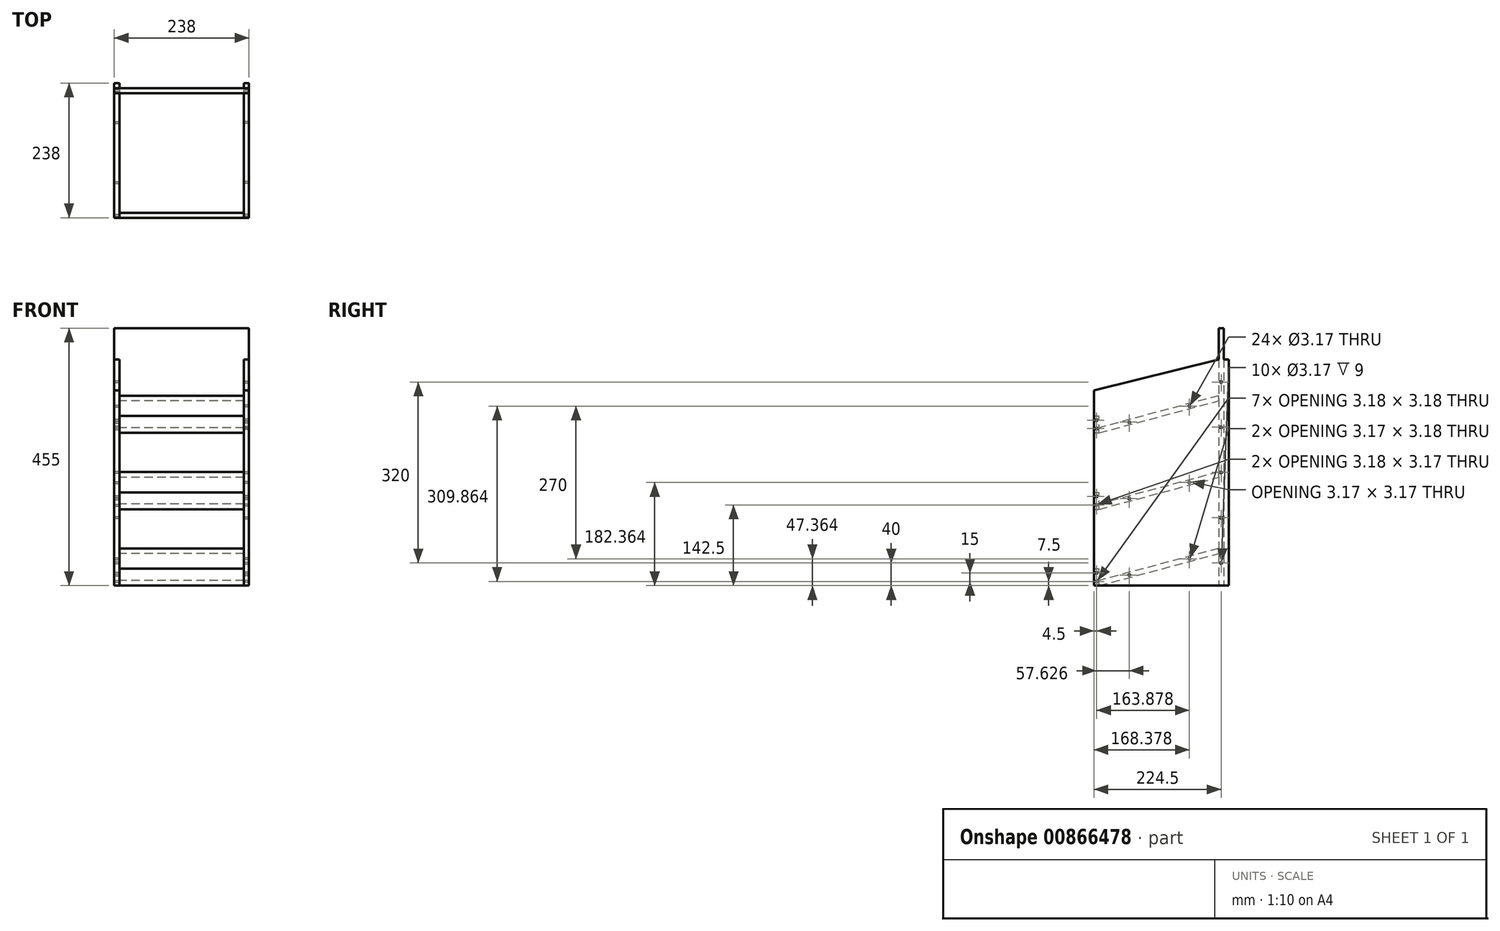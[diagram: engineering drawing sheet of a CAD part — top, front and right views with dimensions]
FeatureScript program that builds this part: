
annotation { "Feature Type Name" : "Feature", "Feature Type Description" : "" }
export const myFeature = defineFeature(function(context is Context, id is Id, definition is map)
    precondition{}
    {
        {
            var Q0;
            Q0=qCreatedBy(makeId("Front.planeOp"),FACE);
            var sketch = newSketch(context, id + "F0", { "sketchPlane" : qUnion([Q0])});
            skLineSegment(sketch, "E0", {"start": v(0, 0) * mm, "end": v(0, -257.67) * mm, "construction": true});
            skLineSegment(sketch, "E1.bottom", {"start": v(110, 165) * mm, "end": v(-110, 165) * mm, "construction": true});
            skLineSegment(sketch, "E1.top", {"start": v(110, -165) * mm, "end": v(-110, -165) * mm, "construction": true});
            skLineSegment(sketch, "E1.left", {"start": v(110, 165) * mm, "end": v(110, -165) * mm, "construction": true});
            skLineSegment(sketch, "E1.right", {"start": v(-110, 165) * mm, "end": v(-110, -165) * mm, "construction": true});
            skPoint(sketch, "E1.middle", {"position": v(0, 0) * mm});
            skLineSegment(sketch, "E2.bottom", {"start": v(-110, -165) * mm, "end": v(-119, -165) * mm});
            skLineSegment(sketch, "E2.top", {"start": v(-110, 235) * mm, "end": v(-119, 235) * mm});
            skLineSegment(sketch, "E2.left", {"start": v(-110, -165) * mm, "end": v(-110, 235) * mm});
            skLineSegment(sketch, "E2.right", {"start": v(-119, -165) * mm, "end": v(-119, 235) * mm});
            skSolve(sketch);
        }
        {
            var Q0;
            Q0=makeQuery(id+"F0.imprint","IMPRINT",FACE,{"disambiguationData":[TD([[makeQuery(id+"F0.imprint","IMPRINT",EDGE,{"derivedFrom":sQuery(id+"F0.wireOp",EDGE,"E2.bottom")}),-1.0]])]});
            var Q1;
            Q1=makeQuery(id+"F0.imprint","IMPRINT",FACE,{"disambiguationData":[TD([[makeQuery(id+"F0.imprint","IMPRINT",EDGE,{"derivedFrom":sQuery(id+"F0.wireOp",EDGE,"DBtvyfOU-g9G0-gBuZ-INMD-cw8ts6dnQgd4.bottom")}),1.0]])]});
            extrude(context, id + "F1", {"entities" : qUnion([Q0, Q1]), "depth" : 238 * mm, "offsetDistance" : 25 * mm});
        }
        {
            var Q0;
            Q0=makeQuery(id+"F1.opExtrude","SWEPT_FACE",FACE,{"disambiguationData":[OSD([sQuery(id+"F0.wireOp",EDGE,"E2.right")])]});
            var sketch = newSketch(context, id + "F2", { "sketchPlane" : qUnion([Q0])});
            skLineSegment(sketch, "E3", {"start": v(238, 235) * mm, "end": v(238, 180) * mm});
            skLineSegment(sketch, "E4", {"start": v(238, 180) * mm, "end": v(18, 235) * mm});
            skLineSegment(sketch, "E5", {"start": v(18, 235) * mm, "end": v(238, 235) * mm});
            skSolve(sketch);
        }
        {
            var Q0;
            Q0=makeQuery(id+"F2.imprint","IMPRINT",FACE,{"disambiguationData":[TD([[makeQuery(id+"F2.imprint","IMPRINT",EDGE,{"derivedFrom":sQuery(id+"F2.wireOp",EDGE,"E3")}),1.0]])]});
            extrude(context, id + "F3", {"entities" : qUnion([Q0]), "operationType" : NewBodyOperationType.REMOVE, "oppositeDirection" : true, "depth" : 10 * mm, "offsetDistance" : 25 * mm});
        }
        {
            var Q0;
            Q0=makeQuery(id+"F1.opExtrude","SWEPT_FACE",FACE,{"disambiguationData":[OSD([sQuery(id+"F0.wireOp",EDGE,"E2.right")])]});
            var sketch = newSketch(context, id + "F4", { "sketchPlane" : qUnion([Q0])});
            skLineSegment(sketch, "E6.bottom", {"start": v(18, 235) * mm, "end": v(9, 235) * mm, "construction": true});
            skLineSegment(sketch, "E6.top", {"start": v(18, -165) * mm, "end": v(9, -165) * mm, "construction": true});
            skLineSegment(sketch, "E6.left", {"start": v(18, 235) * mm, "end": v(18, -165) * mm, "construction": true});
            skLineSegment(sketch, "E6.right", {"start": v(9, 235) * mm, "end": v(9, -165) * mm, "construction": true});
            skCircle(sketch, "E7", {"center": v(13.5, 195) * mm, "radius": 1.59 * mm});
            skCircle(sketch, "E8.0.1.0", {"center": v(13.5, 115) * mm, "radius": 1.59 * mm});
            skCircle(sketch, "E8.0.2.0", {"center": v(13.5, 35) * mm, "radius": 1.59 * mm});
            skLineSegment(sketch, "E8.direction1", {"start": v(13.5, 195) * mm, "end": v(40.5, 195) * mm, "construction": true});
            skLineSegment(sketch, "E8.direction2", {"start": v(13.5, 195) * mm, "end": v(13.5, 115) * mm, "construction": true});
            skCircle(sketch, "E9.0.0.3", {"center": v(13.5, -45) * mm, "radius": 1.59 * mm});
            skCircle(sketch, "E9.0.0.4", {"center": v(13.5, -125) * mm, "radius": 1.59 * mm});
            skSolve(sketch);
        }
        {
            var Q0;
            Q0 = qSketchRegion(id + "F4", true);
            extrude(context, id + "F5", {"entities" : qUnion([Q0]), "operationType" : NewBodyOperationType.REMOVE, "oppositeDirection" : true, "depth" : 9 * mm, "offsetDistance" : 25 * mm});
        }
        {
            var Q0;
            Q0=makeQuery(id+"F1.opExtrude","SWEPT_FACE",FACE,{"disambiguationData":[OSD([sQuery(id+"F0.wireOp",EDGE,"E2.left")])]});
            var sketch = newSketch(context, id + "F6", { "sketchPlane" : qUnion([Q0])});
            skLineSegment(sketch, "E10.bottom", {"start": v(-238, -165) * mm, "end": v(-229, -165) * mm, "construction": true});
            skLineSegment(sketch, "E10.top", {"start": v(-238, 180) * mm, "end": v(-229, 180) * mm, "construction": true});
            skLineSegment(sketch, "E10.left", {"start": v(-238, -165) * mm, "end": v(-238, 180) * mm, "construction": true});
            skLineSegment(sketch, "E10.right", {"start": v(-229, -165) * mm, "end": v(-229, 180) * mm, "construction": true});
            skPoint(sketch, "E11.oppositeSnap0", {"position": v(-9, 235) * mm});
            skLineSegment(sketch, "E11.bottom", {"start": v(-18, 235) * mm, "end": v(-9, 235) * mm, "construction": true});
            skLineSegment(sketch, "E11.top", {"start": v(-18, -165) * mm, "end": v(-9, -165) * mm, "construction": true});
            skLineSegment(sketch, "E11.left", {"start": v(-18, 235) * mm, "end": v(-18, -165) * mm, "construction": true});
            skLineSegment(sketch, "E11.right", {"start": v(-9, 235) * mm, "end": v(-9, -165) * mm, "construction": true});
            skLineSegment(sketch, "E12", {"start": v(-229, -165) * mm, "end": v(-18, -108.46) * mm, "construction": true});
            skLineSegment(sketch, "E13", {"start": v(-229, -155.68) * mm, "end": v(-18, -99.15) * mm, "construction": true});
            skLineSegment(sketch, "E14", {"start": v(-229, -155.68) * mm, "end": v(-229, -165) * mm, "construction": true});
            skLineSegment(sketch, "E15", {"start": v(-18, -99.15) * mm, "end": v(-18, -108.46) * mm, "construction": true});
            skLineSegment(sketch, "E16", {"start": v(-229, -160.34) * mm, "end": v(-18, -103.8) * mm, "construction": true});
            skCircle(sketch, "E17", {"center": v(-175.87, -146.1) * mm, "radius": 1.59 * mm});
            skLineSegment(sketch, "E18", {"start": v(-229, -30) * mm, "end": v(-18, 26.54) * mm, "construction": true});
            skLineSegment(sketch, "E19", {"start": v(-229, -30) * mm, "end": v(-229, -20.68) * mm, "construction": true});
            skLineSegment(sketch, "E20", {"start": v(-229, -20.68) * mm, "end": v(-18, 35.85) * mm, "construction": true});
            skLineSegment(sketch, "E21", {"start": v(-18, 35.85) * mm, "end": v(-18, 26.54) * mm, "construction": true});
            skLineSegment(sketch, "E22", {"start": v(-229, -25.34) * mm, "end": v(-18, 31.2) * mm, "construction": true});
            skCircle(sketch, "E23", {"center": v(-175.87, -11.1) * mm, "radius": 1.59 * mm});
            skLineSegment(sketch, "E24", {"start": v(-229, 105) * mm, "end": v(-18, 161.54) * mm, "construction": true});
            skLineSegment(sketch, "E25", {"start": v(-229, 105) * mm, "end": v(-229, 114.32) * mm, "construction": true});
            skLineSegment(sketch, "E26", {"start": v(-229, 114.32) * mm, "end": v(-18, 170.85) * mm, "construction": true});
            skLineSegment(sketch, "E27", {"start": v(-18, 170.85) * mm, "end": v(-18, 161.54) * mm, "construction": true});
            skLineSegment(sketch, "E28", {"start": v(-229, 109.66) * mm, "end": v(-18, 166.2) * mm, "construction": true});
            skCircle(sketch, "E29", {"center": v(-175.87, 123.9) * mm, "radius": 1.59 * mm});
            skCircle(sketch, "E30", {"center": v(-69.62, 152.36) * mm, "radius": 1.59 * mm});
            skCircle(sketch, "E31", {"center": v(-69.62, 17.36) * mm, "radius": 1.59 * mm});
            skCircle(sketch, "E32", {"center": v(-69.62, -117.64) * mm, "radius": 1.59 * mm});
            skLineSegment(sketch, "E33.bottom", {"start": v(-229, 105) * mm, "end": v(-238, 105) * mm, "construction": true});
            skLineSegment(sketch, "E33.top", {"start": v(-229, 135) * mm, "end": v(-238, 135) * mm, "construction": true});
            skLineSegment(sketch, "E33.left", {"start": v(-229, 105) * mm, "end": v(-229, 135) * mm, "construction": true});
            skLineSegment(sketch, "E33.right", {"start": v(-238, 105) * mm, "end": v(-238, 135) * mm, "construction": true});
            skLineSegment(sketch, "E34.bottom", {"start": v(-229, -30) * mm, "end": v(-238, -30) * mm, "construction": true});
            skLineSegment(sketch, "E34.top", {"start": v(-229, 0) * mm, "end": v(-238, 0) * mm, "construction": true});
            skLineSegment(sketch, "E34.left", {"start": v(-229, -30) * mm, "end": v(-229, 0) * mm, "construction": true});
            skLineSegment(sketch, "E34.right", {"start": v(-238, -30) * mm, "end": v(-238, 0) * mm, "construction": true});
            skLineSegment(sketch, "E35.bottom", {"start": v(-229, -165) * mm, "end": v(-238, -165) * mm, "construction": true});
            skLineSegment(sketch, "E35.top", {"start": v(-229, -135) * mm, "end": v(-238, -135) * mm, "construction": true});
            skLineSegment(sketch, "E35.left", {"start": v(-229, -165) * mm, "end": v(-229, -135) * mm, "construction": true});
            skLineSegment(sketch, "E35.right", {"start": v(-238, -165) * mm, "end": v(-238, -135) * mm, "construction": true});
            skLineSegment(sketch, "E36", {"start": v(-233.5, 135) * mm, "end": v(-233.5, -165) * mm, "construction": true});
            skCircle(sketch, "E37", {"center": v(-233.5, -142.5) * mm, "radius": 1.59 * mm});
            skCircle(sketch, "E38", {"center": v(-233.5, -157.5) * mm, "radius": 1.59 * mm});
            skCircle(sketch, "E39", {"center": v(-233.5, -7.5) * mm, "radius": 1.59 * mm});
            skCircle(sketch, "E40", {"center": v(-233.5, -22.5) * mm, "radius": 1.59 * mm});
            skCircle(sketch, "E41", {"center": v(-233.5, 127.5) * mm, "radius": 1.59 * mm});
            skCircle(sketch, "E42", {"center": v(-233.5, 112.5) * mm, "radius": 1.59 * mm});
            skSolve(sketch);
        }
        {
            var Q0;
            Q0 = qSketchRegion(id + "F6", true);
            extrude(context, id + "F7", {"entities" : qUnion([Q0]), "operationType" : NewBodyOperationType.REMOVE, "oppositeDirection" : true, "depth" : 25 * mm, "offsetDistance" : 25 * mm});
        }
        {
            var Q0;
            Q0=makeQuery(id+"F1.opExtrude","SWEPT_BODY",BODY,{"disambiguationData":[OSD([sQuery(id+"F0.wireOp",EDGE,"E2.bottom"),sQuery(id+"F0.wireOp",EDGE,"E2.top"),sQuery(id+"F0.wireOp",EDGE,"E2.left"),sQuery(id+"F0.wireOp",EDGE,"E2.right")])]});
            var Q1;
            Q1=qCreatedBy(makeId("Right.planeOp"),FACE);
            mirror(context, id + "F8", {"entities" : qUnion([Q0]), "mirrorPlane" : qUnion([Q1])});
        }
        {
            var Q0;
            Q0=makeQuery(id+"F8.opPattern","COPY",FACE,{"derivedFrom":makeQuery(id+"F1.opExtrude","SWEPT_FACE",FACE,{"disambiguationData":[OSD([sQuery(id+"F0.wireOp",EDGE,"E2.bottom")])]}),"instanceName":"1"});
            var sketch = newSketch(context, id + "F9", { "sketchPlane" : qUnion([Q0])});
            skLineSegment(sketch, "E43.bottom", {"start": v(110, 9) * mm, "end": v(-110, 9) * mm});
            skLineSegment(sketch, "E43.top", {"start": v(110, 18) * mm, "end": v(-110, 18) * mm});
            skLineSegment(sketch, "E43.left", {"start": v(110, 9) * mm, "end": v(110, 18) * mm});
            skLineSegment(sketch, "E43.right", {"start": v(-110, 9) * mm, "end": v(-110, 18) * mm});
            skPoint(sketch, "E43.middle", {"position": v(0, 13.5) * mm});
            skSolve(sketch);
        }
        {
            var Q0;
            Q0=makeQuery(id+"F9.imprint","IMPRINT",FACE,{"disambiguationData":[TD([[makeQuery(id+"F9.imprint","IMPRINT",EDGE,{"derivedFrom":sQuery(id+"F9.wireOp",EDGE,"E43.bottom")}),-1.0]])]});
            extrude(context, id + "F10", {"entities" : qUnion([Q0]), "oppositeDirection" : true, "depth" : 400 * mm, "offsetDistance" : 25 * mm});
        }
        {
            var Q0;
            Q0=makeQuery(id+"F10.opExtrude","CAP_FACE",FACE,{"disambiguationData":[OSD([sQuery(id+"F9.wireOp",EDGE,"E43.bottom"),sQuery(id+"F9.wireOp",EDGE,"E43.top"),sQuery(id+"F9.wireOp",EDGE,"E43.left"),sQuery(id+"F9.wireOp",EDGE,"E43.right")])],"isStart":false});
            var sketch = newSketch(context, id + "F11", { "sketchPlane" : qUnion([Q0])});
            skLineSegment(sketch, "E44.bottom", {"start": v(119, -9) * mm, "end": v(-119, -9) * mm});
            skLineSegment(sketch, "E44.top", {"start": v(119, -18) * mm, "end": v(-119, -18) * mm});
            skLineSegment(sketch, "E44.left", {"start": v(119, -9) * mm, "end": v(119, -18) * mm});
            skLineSegment(sketch, "E44.right", {"start": v(-119, -9) * mm, "end": v(-119, -18) * mm});
            skPoint(sketch, "E44.middle", {"position": v(0, -13.5) * mm});
            skPoint(sketch, "E44.middle.positionSnap0", {"position": v(0, -9) * mm});
            skPoint(sketch, "E44.centerSnap0", {"position": v(0, -9) * mm});
            skSolve(sketch);
        }
        {
            var Q0;
            {var subQ1=makeQuery(id+"F10.opExtrude","CAP_EDGE",EDGE,{"disambiguationData":[OSD([sQuery(id+"F9.wireOp",EDGE,"E43.left")])],"isStart":false});Q0=makeQuery(id+"F11.imprint","IMPRINT",FACE,{"disambiguationData":[TD([[makeQuery(id+"F11.imprint","IMPRINT",EDGE,{"derivedFrom":subQ1}),1.0]])]});}
            var Q1;
            {var subQ2=sQuery(id+"F11.wireOp",EDGE,"E44.right");Q1=makeQuery(id+"F11.imprint","IMPRINT",FACE,{"disambiguationData":[TD([[makeQuery(id+"F11.imprint","IMPRINT",EDGE,{"derivedFrom":subQ2}),1.0]])]});}
            var Q2;
            {var subQ2=sQuery(id+"F11.wireOp",EDGE,"E44.left");Q2=makeQuery(id+"F11.imprint","IMPRINT",FACE,{"disambiguationData":[TD([[makeQuery(id+"F11.imprint","IMPRINT",EDGE,{"derivedFrom":subQ2}),-1.0]])]});}
            extrude(context, id + "F12", {"entities" : qUnion([Q0, Q1, Q2]), "operationType" : NewBodyOperationType.ADD, "depth" : 55 * mm, "offsetDistance" : 25 * mm});
        }
        {
            var Q0;
            Q0=makeQuery(id+"F1.opExtrude","SWEPT_FACE",FACE,{"disambiguationData":[OSD([sQuery(id+"F0.wireOp",EDGE,"E2.left")])]});
            var sketch = newSketch(context, id + "F13", { "sketchPlane" : qUnion([Q0])});
            skLineSegment(sketch, "E45.bottom", {"start": v(-238, -165) * mm, "end": v(-229, -165) * mm});
            skLineSegment(sketch, "E45.top", {"start": v(-238, -135) * mm, "end": v(-229, -135) * mm});
            skLineSegment(sketch, "E45.left", {"start": v(-238, -165) * mm, "end": v(-238, -135) * mm});
            skLineSegment(sketch, "E45.right", {"start": v(-229, -165) * mm, "end": v(-229, -135) * mm});
            skLineSegment(sketch, "E46.bottom", {"start": v(-238, -30) * mm, "end": v(-229, -30) * mm});
            skLineSegment(sketch, "E46.top", {"start": v(-238, 0) * mm, "end": v(-229, 0) * mm});
            skLineSegment(sketch, "E46.left", {"start": v(-238, -30) * mm, "end": v(-238, 0) * mm});
            skLineSegment(sketch, "E46.right", {"start": v(-229, -30) * mm, "end": v(-229, 0) * mm});
            skLineSegment(sketch, "E47.bottom", {"start": v(-238, 105) * mm, "end": v(-229, 105) * mm});
            skLineSegment(sketch, "E47.top", {"start": v(-238, 135) * mm, "end": v(-229, 135) * mm});
            skLineSegment(sketch, "E47.left", {"start": v(-238, 105) * mm, "end": v(-238, 135) * mm});
            skLineSegment(sketch, "E47.right", {"start": v(-229, 105) * mm, "end": v(-229, 135) * mm});
            skPoint(sketch, "E48.oppositeSnap0", {"position": v(-9, 235) * mm});
            skLineSegment(sketch, "E48.bottom", {"start": v(-18, 235) * mm, "end": v(-9, 235) * mm, "construction": true});
            skLineSegment(sketch, "E48.top", {"start": v(-18, -165) * mm, "end": v(-9, -165) * mm, "construction": true});
            skLineSegment(sketch, "E48.left", {"start": v(-18, 235) * mm, "end": v(-18, -165) * mm, "construction": true});
            skLineSegment(sketch, "E48.right", {"start": v(-9, 235) * mm, "end": v(-9, -165) * mm, "construction": true});
            skLineSegment(sketch, "E49", {"start": v(-229, -165) * mm, "end": v(-18, -108.46) * mm});
            skLineSegment(sketch, "E50", {"start": v(-18, -108.46) * mm, "end": v(-18, -99.15) * mm});
            skLineSegment(sketch, "E51", {"start": v(-18, -99.15) * mm, "end": v(-229, -155.68) * mm});
            skLineSegment(sketch, "E52", {"start": v(-229, -155.68) * mm, "end": v(-229, -165) * mm});
            skLineSegment(sketch, "E53", {"start": v(-229, -30) * mm, "end": v(-18, 26.54) * mm});
            skLineSegment(sketch, "E54", {"start": v(-18, 26.54) * mm, "end": v(-18, 35.85) * mm});
            skLineSegment(sketch, "E55", {"start": v(-18, 35.85) * mm, "end": v(-229, -20.68) * mm});
            skLineSegment(sketch, "E56", {"start": v(-229, -20.68) * mm, "end": v(-229, -30) * mm});
            skLineSegment(sketch, "E57", {"start": v(-229, 105) * mm, "end": v(-18, 161.54) * mm});
            skLineSegment(sketch, "E58", {"start": v(-18, 161.54) * mm, "end": v(-18, 170.85) * mm});
            skLineSegment(sketch, "E59", {"start": v(-18, 170.85) * mm, "end": v(-229, 114.32) * mm});
            skLineSegment(sketch, "E60", {"start": v(-229, 114.32) * mm, "end": v(-229, 105) * mm});
            skSolve(sketch);
        }
        {
            var Q0;
            Q0=makeQuery(id+"F13.imprint","IMPRINT",FACE,{"disambiguationData":[TD([[makeQuery(id+"F13.imprint","IMPRINT",EDGE,{"derivedFrom":sQuery(id+"F13.wireOp",EDGE,"E45.bottom")}),1.0]])]});
            var Q1;
            Q1=makeQuery(id+"F13.imprint","IMPRINT",FACE,{"disambiguationData":[TD([[makeQuery(id+"F13.imprint","IMPRINT",EDGE,{"derivedFrom":sQuery(id+"F13.wireOp",EDGE,"E46.bottom")}),1.0]])]});
            var Q2;
            Q2=makeQuery(id+"F13.imprint","IMPRINT",FACE,{"disambiguationData":[TD([[makeQuery(id+"F13.imprint","IMPRINT",EDGE,{"derivedFrom":sQuery(id+"F13.wireOp",EDGE,"E47.bottom")}),1.0]])]});
            extrude(context, id + "F14", {"entities" : qUnion([Q0, Q1, Q2]), "depth" : 220 * mm, "offsetDistance" : 25 * mm});
        }
        {
            var Q0;
            Q0=makeQuery(id+"F13.imprint","IMPRINT",FACE,{"disambiguationData":[TD([[makeQuery(id+"F13.imprint","IMPRINT",EDGE,{"derivedFrom":sQuery(id+"F13.wireOp",EDGE,"E57")}),1.0]])]});
            var Q1;
            Q1=makeQuery(id+"F13.imprint","IMPRINT",FACE,{"disambiguationData":[TD([[makeQuery(id+"F13.imprint","IMPRINT",EDGE,{"derivedFrom":sQuery(id+"F13.wireOp",EDGE,"E53")}),1.0]])]});
            var Q2;
            Q2=makeQuery(id+"F13.imprint","IMPRINT",FACE,{"disambiguationData":[TD([[makeQuery(id+"F13.imprint","IMPRINT",EDGE,{"derivedFrom":sQuery(id+"F13.wireOp",EDGE,"E49")}),1.0]])]});
            extrude(context, id + "F15", {"entities" : qUnion([Q0, Q1, Q2]), "depth" : 220 * mm, "offsetDistance" : 25 * mm});
        }
    });
